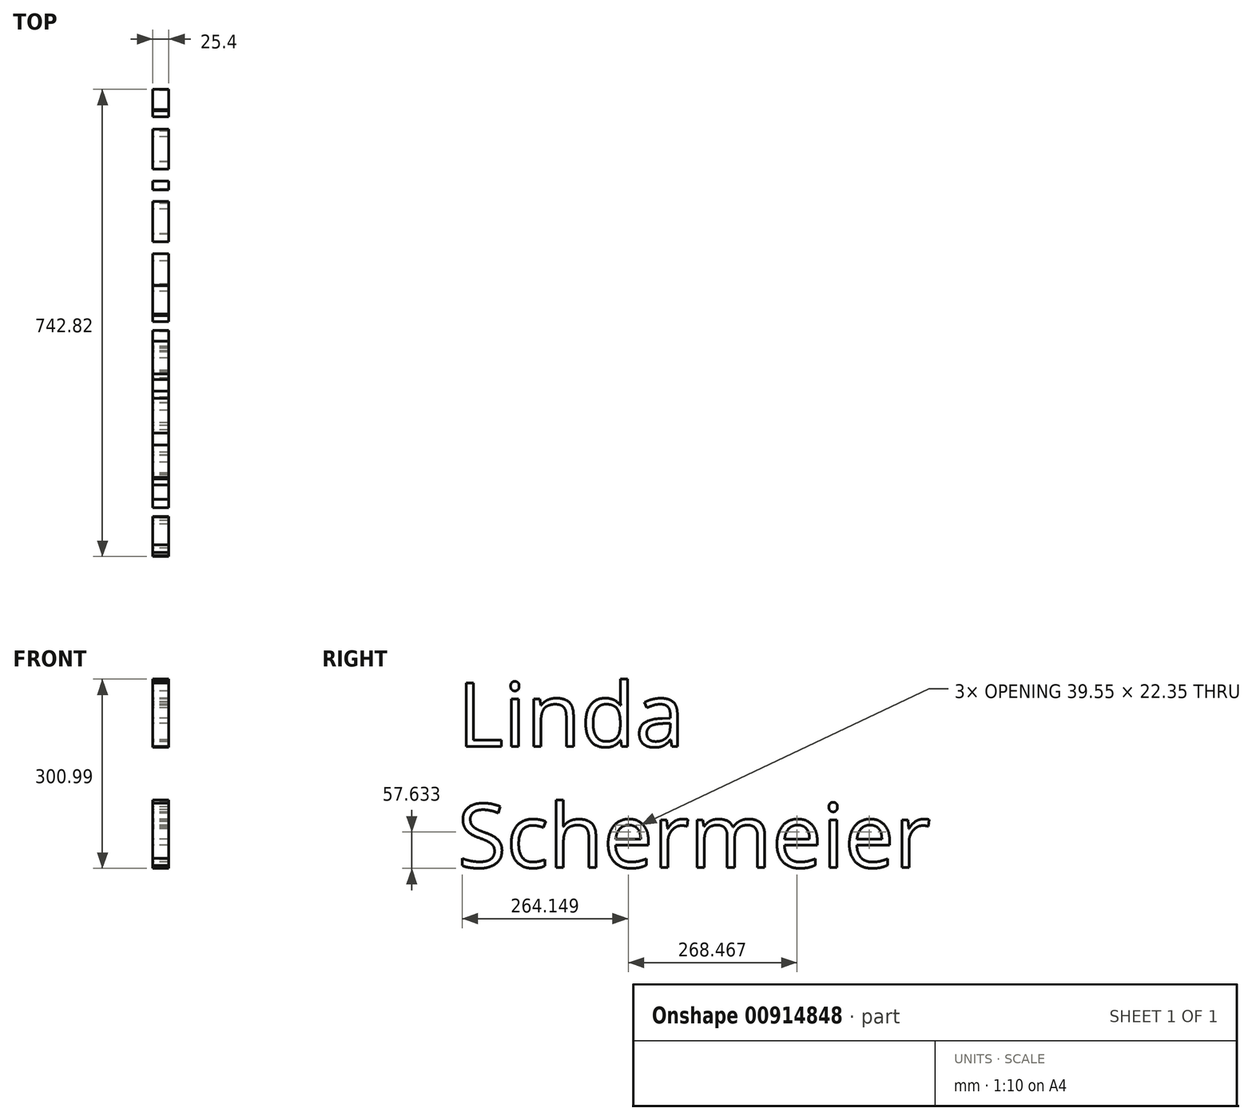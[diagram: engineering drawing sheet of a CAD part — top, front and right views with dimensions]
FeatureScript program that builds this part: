
annotation { "Feature Type Name" : "Feature", "Feature Type Description" : "" }
export const myFeature = defineFeature(function(context is Context, id is Id, definition is map)
    precondition{}
    {
        {
            var Q0;
            Q0=qCreatedBy(makeId("Right.planeOp"),FACE);
            var sketch = newSketch(context, id + "F0", { "sketchPlane" : qUnion([Q0])});
            skText(sketch, "E0", { "text": "Linda\nSchermeier\n", "fontName": "OpenSans-Regular.ttf"});
            const initialGuessF0  = {"E0": [-0.37966, 0, 1, 0, 0.10176]};
            skSetInitialGuess(sketch, initialGuessF0);
            skSolve(sketch);
        }
        {
            var Q0;
            Q0 = qSketchRegion(id + "F0", true);
            extrude(context, id + "F1", {"entities" : qUnion([Q0]), "depth" : 25.4 * mm, "offsetDistance" : 25.4 * mm});
        }
    });
